# Revit family: LoadingDoorProtector_McCue_CSLDP-KIT
name_source: partatom
category: Generic Models
revit_build: Autodesk Revit 2015 (Build: 20140606_1530(x64)
units: mm (PartAtom-declared; Revit-internal decimal feet)

## types (1)
- 52" Length
    Construction Details = http://www.mccue.com
    Cost = 0 $
    Description = McCue CSLDP KIT Loading Door Protector
    Green Building-LEED = http://www.arcat.com
    Horizontal Extension = 51 187/256"
    Installation-Fabrication = http://www.mccue.com
    Keynote = 10 26 23.13
    Manufacturer = McCue Corporation
    Manufacturer Fax = (978) 741-2542
    Manufacturer Website = https://mccue.com
    Model = CSLDP-KIT
    Product Data = http://www.arcat.com
    Protector Material = McCue 307 Yellow
    Revision = R1_2018-01
    Sales Information = http://www.mccue.com
    Specification = http://www.arcat.com
    URL = http://www.mccue.com
    Vertical Extension = 49 59/64"
    Width = 1 1/2"

## geometry (parser evidence)
native form markers: Sweep x17
no freeform markers — native parametric forms only
